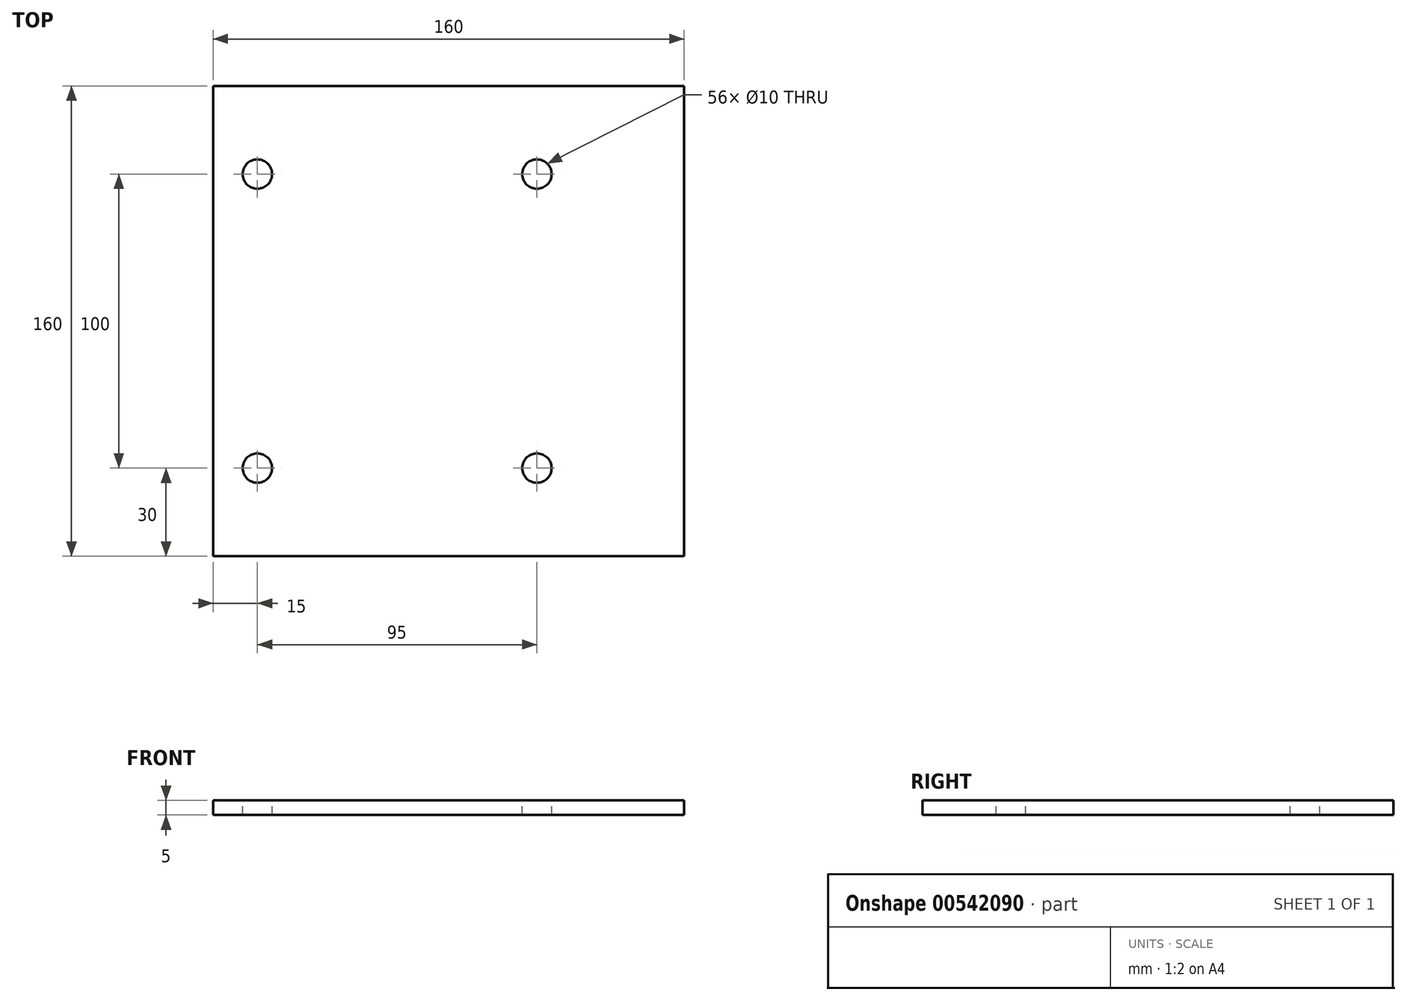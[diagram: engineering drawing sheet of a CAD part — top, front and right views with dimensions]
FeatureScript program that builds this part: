
annotation { "Feature Type Name" : "Feature", "Feature Type Description" : "" }
export const myFeature = defineFeature(function(context is Context, id is Id, definition is map)
    precondition{}
    {
        {
            var Q0;
            Q0=qCreatedBy(makeId("Top.planeOp"),FACE);
            var sketch = newSketch(context, id + "F0", { "sketchPlane" : qUnion([Q0])});
            skLineSegment(sketch, "E0.bottom", {"start": v(-160, 0) * mm, "end": v(0, 0) * mm});
            skLineSegment(sketch, "E0.top", {"start": v(-160, 160) * mm, "end": v(0, 160) * mm});
            skLineSegment(sketch, "E0.left", {"start": v(-160, 0) * mm, "end": v(-160, 160) * mm});
            skLineSegment(sketch, "E0.right", {"start": v(0, 0) * mm, "end": v(0, 160) * mm});
            skSolve(sketch);
        }
        {
            var Q0;
            Q0 = qSketchRegion(id + "F0", true);
            extrude(context, id + "F1", {"entities" : qUnion([Q0]), "depth" : 5 * mm, "offsetDistance" : 25.4 * mm});
        }
        {
            var Q0;
            Q0=makeQuery(id+"F1.opExtrude","CAP_FACE",FACE,{"disambiguationData":[OSD([sQuery(id+"F0.wireOp",EDGE,"E0.bottom"),sQuery(id+"F0.wireOp",EDGE,"E0.top"),sQuery(id+"F0.wireOp",EDGE,"E0.left"),sQuery(id+"F0.wireOp",EDGE,"E0.right")])],"isStart":false});
            var sketch = newSketch(context, id + "F2", { "sketchPlane" : qUnion([Q0])});
            skPoint(sketch, "E1", {"position": v(-50, 30) * mm});
            skPoint(sketch, "E2.0.1.0", {"position": v(-50, 130) * mm});
            skPoint(sketch, "E2.1.0.0", {"position": v(-145, 30) * mm});
            skPoint(sketch, "E2.1.1.0", {"position": v(-145, 130) * mm});
            skLineSegment(sketch, "E2.direction1", {"start": v(-50, 30) * mm, "end": v(-145, 30) * mm, "construction": true});
            skLineSegment(sketch, "E2.direction2", {"start": v(-50, 30) * mm, "end": v(-50, 130) * mm, "construction": true});
            skSolve(sketch);
        }
        {
            var Q0;
            Q0=sQuery(id+"F2.wireOp",VERTEX,"E1");
            var Q1;
            Q1=sQuery(id+"F2.wireOp",VERTEX,"E2.1.0.0");
            var Q2;
            Q2=sQuery(id+"F2.wireOp",VERTEX,"E2.0.1.0");
            var Q3;
            Q3=sQuery(id+"F2.wireOp",VERTEX,"E2.1.1.0");
            var Q4;
            Q4=makeQuery(id+"F1.opExtrude","SWEPT_BODY",BODY,{"disambiguationData":[OSD([sQuery(id+"F0.wireOp",EDGE,"E0.bottom"),sQuery(id+"F0.wireOp",EDGE,"E0.top"),sQuery(id+"F0.wireOp",EDGE,"E0.left"),sQuery(id+"F0.wireOp",EDGE,"E0.right")])]});
            hole(context, id + "F3", {"style" : HoleStyle.SIMPLE, "endStyle" : HoleEndStyle.THROUGH, "holeDiameter" : 10 * mm, "isTappedThrough" : true, "tappedDepth" : 12.7 * mm, "tapClearance" : 3, "locations" : qUnion([Q0, Q1, Q2, Q3]), "scope" : qUnion([Q4])});
        }
    });
